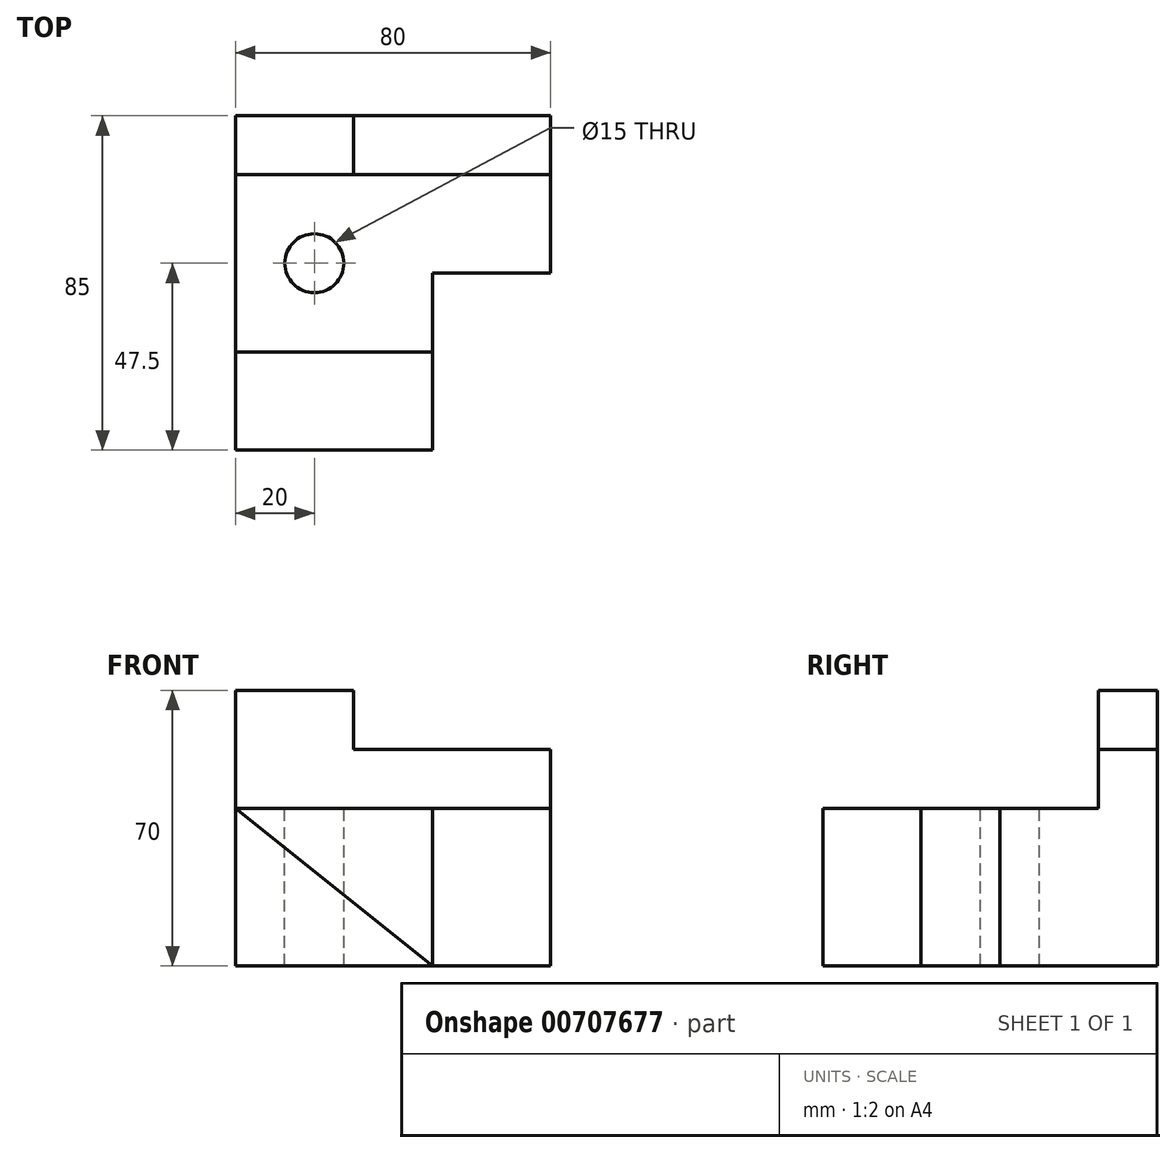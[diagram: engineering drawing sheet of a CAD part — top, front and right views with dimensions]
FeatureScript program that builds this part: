
annotation { "Feature Type Name" : "Feature", "Feature Type Description" : "" }
export const myFeature = defineFeature(function(context is Context, id is Id, definition is map)
    precondition{}
    {
        {
            var Q0;
            Q0=qCreatedBy(makeId("Front.planeOp"),FACE);
            var sketch = newSketch(context, id + "F0", { "sketchPlane" : qUnion([Q0])});
            skLineSegment(sketch, "E0", {"start": v(0, 0) * mm, "end": v(0, 40) * mm});
            skLineSegment(sketch, "E1", {"start": v(0, 0) * mm, "end": v(50, 0) * mm});
            skLineSegment(sketch, "E2", {"start": v(0, 40) * mm, "end": v(50, 0) * mm});
            skSolve(sketch);
        }
        {
            var Q0;
            Q0 = qSketchRegion(id + "F0", true);
            extrude(context, id + "F1", {"entities" : qUnion([Q0]), "oppositeDirection" : true, "depth" : 25 * mm, "offsetDistance" : 25 * mm});
        }
        {
            var Q0;
            Q0=qCreatedBy(makeId("Top.planeOp"),FACE);
            var sketch = newSketch(context, id + "F2", { "sketchPlane" : qUnion([Q0])});
            skLineSegment(sketch, "E3", {"start": v(0, 25) * mm, "end": v(0, 70) * mm});
            skLineSegment(sketch, "E4", {"start": v(0, 70) * mm, "end": v(80, 70) * mm});
            skLineSegment(sketch, "E5", {"start": v(80, 70) * mm, "end": v(80, 45) * mm});
            skLineSegment(sketch, "E6", {"start": v(0, 25) * mm, "end": v(50, 25) * mm});
            skLineSegment(sketch, "E7", {"start": v(50, 25) * mm, "end": v(50, 45) * mm});
            skLineSegment(sketch, "E8", {"start": v(50, 45) * mm, "end": v(80, 45) * mm});
            skSolve(sketch);
        }
        {
            var Q0;
            Q0 = qSketchRegion(id + "F2", true);
            extrude(context, id + "F3", {"entities" : qUnion([Q0]), "operationType" : NewBodyOperationType.ADD, "depth" : 40 * mm, "offsetDistance" : 25 * mm});
        }
        {
            var Q0;
            Q0=makeQuery(id+"F3.opExtrude","SWEPT_FACE",FACE,{"disambiguationData":[OSD([sQuery(id+"F2.wireOp",EDGE,"E4")])]});
            var sketch = newSketch(context, id + "F4", { "sketchPlane" : qUnion([Q0])});
            skLineSegment(sketch, "E9", {"start": v(0, 0) * mm, "end": v(0, 70) * mm});
            skLineSegment(sketch, "E10", {"start": v(0, 70) * mm, "end": v(-30, 70) * mm});
            skLineSegment(sketch, "E11", {"start": v(-30, 70) * mm, "end": v(-30, 55) * mm});
            skLineSegment(sketch, "E12", {"start": v(-30, 55) * mm, "end": v(-80, 55) * mm});
            skLineSegment(sketch, "E13", {"start": v(-80, 55) * mm, "end": v(-80, 40) * mm});
            skLineSegment(sketch, "E14", {"start": v(-80, 40) * mm, "end": v(-80, 0) * mm});
            skLineSegment(sketch, "E15", {"start": v(-80, 0) * mm, "end": v(2.17, 0) * mm});
            skSolve(sketch);
        }
        {
            var Q0;
            Q0 = qSketchRegion(id + "F4", true);
            extrude(context, id + "F5", {"entities" : qUnion([Q0]), "operationType" : NewBodyOperationType.ADD, "depth" : 15 * mm, "offsetDistance" : 25 * mm});
        }
        {
            var Q0;
            Q0=makeQuery(id+"F3.opExtrude","CAP_FACE",FACE,{"disambiguationData":[OSD([sQuery(id+"F2.wireOp",EDGE,"E3"),sQuery(id+"F2.wireOp",EDGE,"E4"),sQuery(id+"F2.wireOp",EDGE,"E5"),sQuery(id+"F2.wireOp",EDGE,"E6"),sQuery(id+"F2.wireOp",EDGE,"E7"),sQuery(id+"F2.wireOp",EDGE,"E8")])],"isStart":false});
            var sketch = newSketch(context, id + "F6", { "sketchPlane" : qUnion([Q0])});
            skLineSegment(sketch, "E16", {"start": v(0, 0) * mm, "end": v(0, 47.5) * mm});
            skLineSegment(sketch, "E17", {"start": v(0, 47.5) * mm, "end": v(20, 47.5) * mm});
            skCircle(sketch, "E18", {"center": v(20, 47.5) * mm, "radius": 7.5 * mm});
            skSolve(sketch);
        }
        {
            var Q0;
            Q0=makeQuery(id+"F6.imprint","IMPRINT",FACE,{"disambiguationData":[TD([[makeQuery(id+"F6.imprint","IMPRINT",EDGE,{"derivedFrom":sQuery(id+"F6.wireOp",EDGE,"E18")}),1.0]])]});
            extrude(context, id + "F7", {"entities" : qUnion([Q0]), "operationType" : NewBodyOperationType.REMOVE, "oppositeDirection" : true, "depth" : 40 * mm, "offsetDistance" : 25 * mm});
        }
    });
